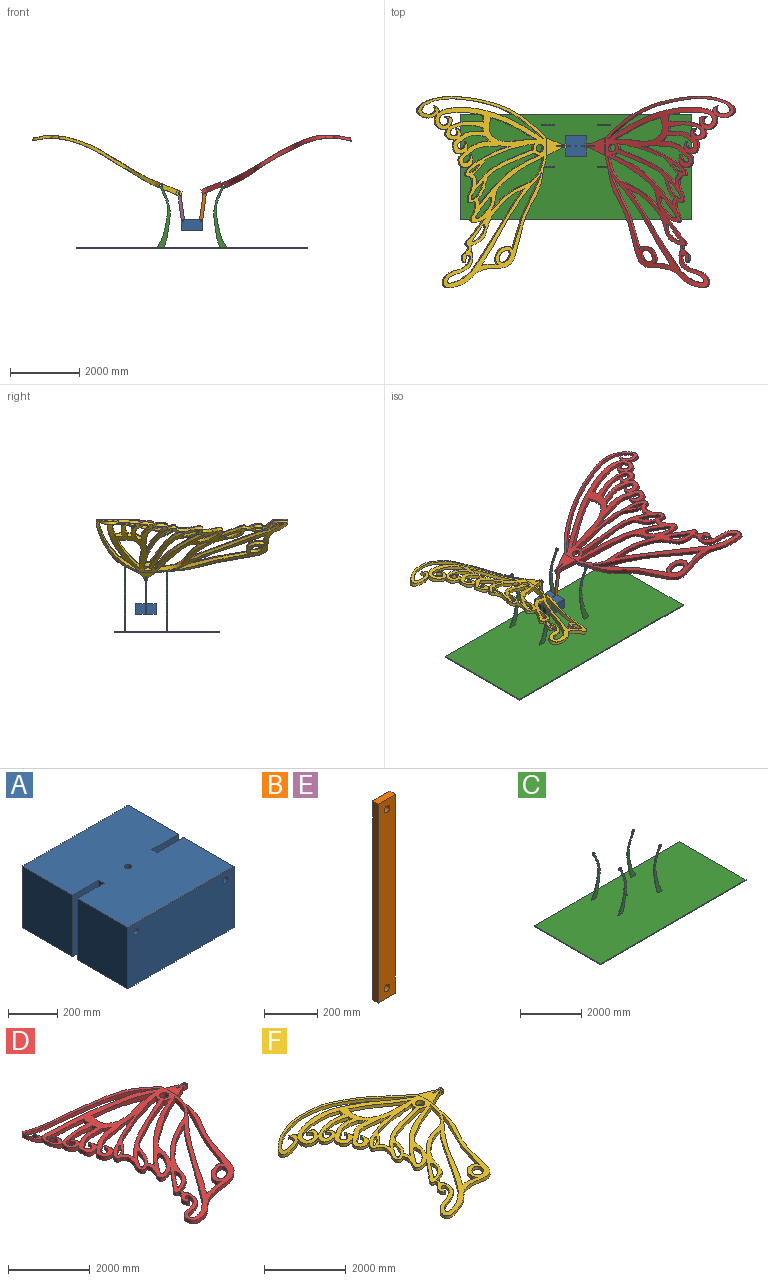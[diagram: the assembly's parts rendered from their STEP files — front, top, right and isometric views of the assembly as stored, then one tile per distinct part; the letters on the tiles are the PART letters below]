
ASSEMBLY  parts=6 mates=12
PART A: 19 faces, bbox 609.6x609.6x304.8 mm
  f0: plane 304.8x289.56mm, normal (1,0,0), area 88257.9mm2, adj f4,f6,f7,f15
  f1: plane 304.8x289.56mm, normal (-1,0,0), area 88257.9mm2, adj f4,f6,f7,f11
  f2: plane 609.6x304.8mm, normal (0,1,0), area 184346.8mm2, adj f3,f5,f6,f7,f13,f17
  f3: plane 304.8x289.56mm, normal (-1,0,0), area 88257.9mm2, adj f2,f6,f7,f10
  f4: plane 609.6x304.8mm, normal (0,-1,0), area 184346.8mm2, adj f0,f1,f6,f7,f12,f18
  f5: plane 304.8x289.56mm, normal (1,0,0), area 88257.9mm2, adj f2,f6,f7,f16
  f6: plane 609.6x609.6mm, normal (0,0,1), area 361592.2mm2, adj f0,f1,f2,f3,f4,f5,f8,f9
  f7: plane 609.6x609.6mm, normal (0,0,-1), area 361592.2mm2, adj f0,f1,f2,f3,f4,f5,f8,f9
  f8: cylinder r=15.24mm len=304.8mm, axis (0,0,1), area 29186.4mm2, adj f6,f7
  f9: plane 304.8x30.48mm, normal (-1,0,0), area 9290.3mm2, adj f6,f7,f10,f11
  f10: plane 304.8x152.4mm, normal (0,-1,0), area 45721.9mm2, adj f3,f6,f7,f9,f13
  f11: plane 304.8x152.4mm, normal (0,1,0), area 45721.9mm2, adj f1,f6,f7,f9,f12
  f12: cylinder r=15.24mm len=289.56mm, axis (0,-1,0), area 27727mm2, adj f4,f11
  f13: cylinder r=15.24mm len=289.56mm, axis (0,-1,0), area 27727mm2, adj f2,f10
  f14: plane 304.8x30.48mm, normal (1,0,0), area 9290.3mm2, adj f6,f7,f15,f16
  f15: plane 304.8x152.4mm, normal (0,1,0), area 45721.9mm2, adj f0,f6,f7,f14,f18
  f16: plane 304.8x152.4mm, normal (0,-1,0), area 45721.9mm2, adj f5,f6,f7,f14,f17
  f17: cylinder r=15.24mm len=289.56mm, axis (0,-1,0), area 27727mm2, adj f2,f16
  f18: cylinder r=15.24mm len=289.56mm, axis (0,-1,0), area 27727mm2, adj f4,f15
PART B: 8 faces, bbox 91.4x30.5x914.4 mm
  f0: plane 914.4x30.48mm, normal (-1,0,0), area 27870.9mm2, adj f1,f3,f4,f5
  f1: plane 91.44x30.48mm, normal (0,0,-1), area 2787.1mm2, adj f0,f2,f4,f5
  f2: plane 914.4x30.48mm, normal (1,0,0), area 27870.9mm2, adj f1,f3,f4,f5
  f3: plane 91.44x30.48mm, normal (0,0,1), area 2787.1mm2, adj f0,f2,f4,f5
  f4: plane 914.4x91.44mm, normal (0,-1,0), area 82153.4mm2, adj f0,f1,f2,f3,f6,f7
  f5: plane 914.4x91.44mm, normal (0,1,0), area 82153.4mm2, adj f0,f1,f2,f3,f6,f7
  f6: cylinder r=15.24mm len=30.48mm, axis (0,-1,0), area 2918.6mm2, adj f4,f5
  f7: cylinder r=15.24mm len=30.48mm, axis (0,-1,0), area 2918.6mm2, adj f4,f5
PART C: 31 faces, bbox 6705.6x3048x1884.5 mm
  f0: extruded ~1753.07x293.63mm, area 56280.8mm2, adj f9,f10,f11,f16
  f1: extruded ~1753.07x293.63mm, area 56280.8mm2, adj f2,f4,f5,f16
  f2: cylinder r=51.08mm len=102.17mm, axis (0,1,0), area 8054.2mm2, adj f1,f4,f5,f6
  f3: cylinder r=25.91mm len=51.82mm, axis (0,1,0), area 4961.7mm2, adj f4,f5
  f4: plane 1863.69x392.01mm, normal (0,-1,0), area 178526.9mm2, adj f1,f2,f3,f6,f16
  f5: plane 1863.69x392.01mm, normal (0,1,0), area 178526.9mm2, adj f1,f2,f3,f6,f16
  f6: extruded ~1771.07x243.88mm, area 56045.9mm2, adj f2,f4,f5,f16
  f7: extruded ~1771.07x243.88mm, area 56045.9mm2, adj f9,f10,f11,f16
  f8: cylinder r=25.91mm len=51.82mm, axis (0,1,0), area 4961.7mm2, adj f10,f11
  f9: cylinder r=51.08mm len=102.17mm, axis (0,1,0), area 8054.2mm2, adj f0,f7,f10,f11
  f10: plane 1863.69x392.01mm, normal (0,1,0), area 178526.9mm2, adj f0,f7,f8,f9,f16
  f11: plane 1863.69x392.01mm, normal (0,-1,0), area 178526.9mm2, adj f0,f7,f8,f9,f16
  f12: plane 6705.6x30.48mm, normal (0,1,0), area 204386.7mm2, adj f13,f15,f16,f17
  f13: plane 3048x30.48mm, normal (-1,0,0), area 92903mm2, adj f12,f14,f16,f17
  f14: plane 6705.6x30.48mm, normal (0,-1,0), area 204386.7mm2, adj f13,f15,f16,f17
  f15: plane 3048x30.48mm, normal (1,0,0), area 92903mm2, adj f12,f14,f16,f17
  f16: plane 6705.6x3048mm, normal (0,0,1), area 20414616.9mm2, adj f0,f1,f4,f5,f6,f7,f10,f11
  f17: plane 6705.6x3048mm, normal (0,0,-1), area 20437939.1mm2, adj f12,f13,f14,f15,f30
  f18: cylinder r=25.91mm len=51.82mm, axis (0,1,0), area 4961.7mm2, adj f20,f21
  f19: cylinder r=51.08mm len=102.17mm, axis (0,1,0), area 8054.2mm2, adj f20,f21,f22,f23
  f20: plane 1863.69x392.01mm, normal (0,-1,0), area 178526.9mm2, adj f16,f18,f19,f22,f23
  f21: plane 1863.69x392.01mm, normal (0,1,0), area 178526.9mm2, adj f16,f18,f19,f22,f23
  f22: extruded ~1753.07x293.63mm, area 56280.8mm2, adj f16,f19,f20,f21
  f23: extruded ~1771.07x243.88mm, area 56045.9mm2, adj f16,f19,f20,f21
  f24: cylinder r=25.91mm len=51.82mm, axis (0,1,0), area 4961.7mm2, adj f26,f27
  f25: cylinder r=51.08mm len=102.17mm, axis (0,1,0), area 8054.2mm2, adj f26,f27,f28,f29
  f26: plane 1863.69x392.01mm, normal (0,-1,0), area 178526.9mm2, adj f16,f24,f25,f28,f29
  f27: plane 1863.69x392.01mm, normal (0,1,0), area 178526.9mm2, adj f16,f24,f25,f28,f29
  f28: extruded ~1753.07x293.63mm, area 56280.8mm2, adj f16,f25,f26,f27
  f29: extruded ~1771.07x243.88mm, area 56045.9mm2, adj f16,f25,f26,f27
  f30: cylinder r=15.24mm len=30.48mm, axis (0,0,1), area 2918.6mm2, adj f16,f17
PART D: 77 faces, bbox 4569.8x5546.8x559 mm
  f0: plane 139.67x42.26mm, normal (1,0,0), area 5902.2mm2, adj f1,f2,f70,f76
  f1: plane 43.55x42.26mm, normal (0,0,1), area 1840.2mm2, adj f0,f3,f70,f76
  f2: plane 609.6x515.81mm, normal (0,0,-1), area 149908.3mm2, adj f0,f7,f68,f69,f70,f71,f72,f74
  f3: cylinder r=22.11mm len=44.21mm, axis (0,-1,0), area 3151mm2, adj f1,f4,f70,f76
  f4: plane 522.13x515.81mm, normal (0,0,1), area 143171.3mm2, adj f3,f8,f69,f70,f71,f72,f73,f74
  f5: plane 168.1x3.34mm, normal (0,-1,0), area 560.2mm2, adj f8,f23,f24,f25,f71
  f6: plane 43.55x34.77mm, normal (0,0,1), area 1514mm2, adj f7,f72,f73,f74
  f7: plane 139.67x34.77mm, normal (1,0,0), area 4855.7mm2, adj f2,f6,f72,f74
  f8: plane 515.81x80.92mm, normal (1,0,0), area 41737.8mm2, adj f4,f5,f9,f24
  f9: extruded ~3956.8x1202.56mm, area 587895.1mm2, adj f8,f10,f24,f25,f67,f69
  f10: extruded ~436.38x335.61mm, area 66062.4mm2, adj f9,f11,f24,f25
  f11: extruded ~324.15x297.79mm, area 60402.2mm2, adj f10,f13,f24,f25
  f12: extruded ~1341.39x636.81mm, area 328183.2mm2, adj f13,f14,f24,f25
  f13: extruded ~408.33x341.3mm, area 78664.2mm2, adj f11,f12,f24,f25
  f14: extruded ~320.07x163.65mm, area 32793.2mm2, adj f12,f16,f24,f25
  f15: extruded ~417.12x114.44mm, area 49528.4mm2, adj f16,f18,f24,f25
  f16: extruded ~1456.29x862.43mm, area 201626.3mm2, adj f14,f15,f24,f25
  f17: extruded ~338.56x112.28mm, area 38376.2mm2, adj f18,f19,f24,f25
  f18: extruded ~360.96x210.21mm, area 60721.4mm2, adj f15,f17,f24,f25
  f19: extruded ~451.34x277.08mm, area 82405.2mm2, adj f17,f21,f24,f25
  f20: extruded ~203.85x113.79mm, area 25603.5mm2, adj f21,f22,f24,f25
  f21: extruded ~810.37x610.36mm, area 119713.7mm2, adj f19,f20,f24,f25
  f22: extruded ~3492.14x3205.76mm, area 891755.8mm2, adj f20,f23,f24,f25
  f23: extruded ~334.69x167.83mm, area 49828.8mm2, adj f5,f22,f24,f25,f67
  f24: extruded ~5546.84x3960.16mm, area 5019713.7mm2, adj f5,f8,f9,f10,f11,f12,f13,f14
  f25: extruded ~5546.85x3960.15mm, area 5068319.2mm2, adj f5,f9,f10,f11,f12,f13,f14,f15
  f26: extruded ~371.73x350.29mm, area 115711.3mm2, adj f24,f25
  f27: extruded ~2698.77x1981.3mm, area 417691.2mm2, adj f24,f25,f29,f30
  f28: extruded ~564.75x514.56mm, area 103093.6mm2, adj f24,f25,f29,f30
  f29: extruded ~2226.78x939.05mm, area 348502.3mm2, adj f24,f25,f27,f28
  f30: extruded ~568.22x174.76mm, area 64613.8mm2, adj f24,f25,f27,f28
  f31: extruded ~175.85x107.14mm, area 19002.5mm2, adj f24,f25,f33,f34
  f32: extruded ~2372.54x1724.5mm, area 334983.2mm2, adj f24,f25,f33,f34
  f33: extruded ~1759.33x1643.13mm, area 287026.4mm2, adj f24,f25,f31,f32
  f34: extruded ~918.64x761.89mm, area 237950.4mm2, adj f24,f25,f31,f32
  f35: extruded ~486.75x409.01mm, area 149049.4mm2, adj f24,f25
  f36: extruded ~1341.6x837.92mm, area 193559.6mm2, adj f24,f25,f37,f38
  f37: extruded ~725.86x386.03mm, area 131874.2mm2, adj f24,f25,f36,f38
  f38: extruded ~1727.64x1563.78mm, area 306702.1mm2, adj f24,f25,f36,f37
  f39: extruded ~112.15x30.15mm, area 4263.4mm2, adj f24,f25,f40
  f40: extruded ~507.41x388.55mm, area 143500.5mm2, adj f24,f25,f39
  f41: cylinder r=204.59mm len=159.75mm, axis (0,0,-1), area 26058.5mm2, adj f24,f25,f43,f44
  f42: extruded ~190.19x115.16mm, area 21877.8mm2, adj f24,f25,f43,f44
  f43: extruded ~1985.13x1436.63mm, area 305854mm2, adj f24,f25,f41,f42
  f44: extruded ~1874.18x1314.28mm, area 293259.9mm2, adj f24,f25,f41,f42
  f45: extruded ~606.27x529.22mm, area 191510.7mm2, adj f24,f25
  f46: extruded ~290.04x177.88mm, area 45404.1mm2, adj f24,f25,f47,f50
  f47: cylinder r=204.59mm len=167.51mm, axis (0,0,-1), area 27142.2mm2, adj f24,f25,f46,f49
  f48: extruded ~295.93x114.32mm, area 36439.4mm2, adj f24,f25,f49,f50
  f49: extruded ~1894.48x1013.51mm, area 262807.4mm2, adj f24,f25,f47,f48
  f50: extruded ~1745.39x844.81mm, area 230263.9mm2, adj f24,f25,f46,f48
  f51: extruded ~312.12x250.36mm, area 91397mm2, adj f24,f25
  f52: extruded ~745.31x256.52mm, area 89734.6mm2, adj f24,f25,f53,f54
  f53: extruded ~874.58x425.82mm, area 183377mm2, adj f24,f25,f52,f54
  f54: extruded ~160.33x146.95mm, area 25272.4mm2, adj f24,f25,f52,f53
  f55: extruded ~727.11x153.38mm, area 82853.4mm2, adj f24,f25,f56,f57
  f56: extruded ~1000.21x334.31mm, area 207702.3mm2, adj f24,f25,f55,f57
  f57: extruded ~128.26x117.18mm, area 15039.6mm2, adj f24,f25,f55,f56
  f58: extruded ~1027.59x151.94mm, area 115311.2mm2, adj f24,f25,f59,f60
  f59: extruded ~1342.84x408.07mm, area 267599.7mm2, adj f24,f25,f58,f60
  f60: extruded ~193.21x117.8mm, area 22533.7mm2, adj f24,f25,f58,f59
  f61: cylinder r=111mm len=222.01mm, axis (0,0,-1), area 108573.6mm2, adj f24,f25
  f62: extruded ~1571.66x697.24mm, area 254753.4mm2, adj f24,f25,f63
  f63: extruded ~1515.88x632.2mm, area 207996mm2, adj f24,f25,f62
  f64: extruded ~3775.49x1155.09mm, area 548964.1mm2, adj f24,f25,f65,f66
  f65: extruded ~206.26x146.99mm, area 24674.3mm2, adj f24,f25,f64,f66
  f66: extruded ~3350.46x907.58mm, area 430785.2mm2, adj f24,f25,f64,f65
  f67: cylinder r=24.38mm len=859.93mm, axis (0,-1,0), area 114966.2mm2, adj f9,f23
  f68: plane 515.81x52.49mm, normal (-1,0,0), area 27075mm2, adj f2,f25,f69,f71
  f69: plane 456.44x178.06mm, normal (0.36,0.93,0), area 68430.7mm2, adj f2,f4,f9,f68,f70
  f70: plane 153.16x139.67mm, normal (0,1,0), area 20511.9mm2, adj f0,f1,f2,f3,f4,f69
  f71: plane 460.62x230.25mm, normal (0.45,-0.89,0), area 71925.1mm2, adj f2,f4,f5,f68,f72
  f72: plane 148.98x139.67mm, normal (0,-1,0), area 19928.3mm2, adj f2,f4,f6,f7,f71,f73
  f73: cylinder r=22.11mm len=44.21mm, axis (0,-1,0), area 2592.3mm2, adj f4,f6,f72,f74
  f74: plane 304.8x139.67mm, normal (0,1,0), area 41691.6mm2, adj f2,f4,f6,f7,f73,f75
  f75: plane 139.67x30.48mm, normal (1,0,0), area 4257.2mm2, adj f2,f4,f74,f76
  f76: plane 304.8x139.67mm, normal (0,-1,0), area 41691.6mm2, adj f0,f1,f2,f3,f4,f75
PART E: same geometry as B
PART F: 73 faces, bbox 4569.8x5546.8x534.1 mm
  f0: plane 139.67x43.35mm, normal (1,0,0), area 6054.7mm2, adj f3,f4,f68,f71
  f1: cylinder r=22.11mm len=44.21mm, axis (0,-1,0), area 6021.4mm2, adj f68,f71
  f2: plane 139.67x3.34mm, normal (0,-1,0), area 465.5mm2, adj f20,f21,f22,f67
  f3: plane 609.6x515.81mm, normal (0,0,1), area 149908.3mm2, adj f0,f5,f21,f65,f66,f67,f68,f70
  f4: plane 609.6x515.81mm, normal (0,0,-1), area 149908.3mm2, adj f0,f5,f22,f65,f66,f67,f68,f70
  f5: plane 139.67x33.67mm, normal (1,0,0), area 4703.2mm2, adj f3,f4,f66,f70
  f6: extruded ~3956.8x1202.56mm, area 479492.5mm2, adj f7,f21,f22,f64,f65
  f7: extruded ~436.38x335.61mm, area 59997.6mm2, adj f6,f8,f21,f22
  f8: extruded ~324.15x297.79mm, area 45490mm2, adj f7,f10,f21,f22
  f9: extruded ~1341.39x636.81mm, area 262319.7mm2, adj f10,f11,f21,f22
  f10: extruded ~408.33x341.3mm, area 55795.2mm2, adj f8,f9,f21,f22
  f11: extruded ~320.07x139.67mm, area 30654.5mm2, adj f9,f13,f21,f22
  f12: extruded ~417.12x114.44mm, area 41974.9mm2, adj f13,f15,f21,f22
  f13: extruded ~1456.29x862.43mm, area 170075.6mm2, adj f11,f12,f21,f22
  f14: extruded ~338.56x95.61mm, area 33270.6mm2, adj f15,f16,f21,f22
  f15: extruded ~360.96x210.21mm, area 50245.5mm2, adj f12,f14,f21,f22
  f16: extruded ~451.34x277.08mm, area 69924.5mm2, adj f14,f18,f21,f22
  f17: extruded ~203.85x113.79mm, area 20376.9mm2, adj f18,f19,f21,f22
  f18: extruded ~810.37x610.36mm, area 99648.6mm2, adj f16,f17,f21,f22
  f19: extruded ~3492.14x3205.76mm, area 673396.6mm2, adj f17,f20,f21,f22
  f20: extruded ~334.69x139.47mm, area 40369.6mm2, adj f2,f19,f21,f22,f64
  f21: extruded ~5546.84x3960.15mm, area 4961774.6mm2, adj f2,f3,f6,f7,f8,f9,f10,f11
  f22: extruded ~5546.84x3960.13mm, area 5066569.9mm2, adj f2,f4,f6,f7,f8,f9,f10,f11
  f23: extruded ~371.73x350.29mm, area 107130.3mm2, adj f21,f22
  f24: extruded ~2698.77x1981.3mm, area 327186.9mm2, adj f21,f22,f26,f27
  f25: extruded ~564.75x514.56mm, area 91953.3mm2, adj f21,f22,f26,f27
  f26: extruded ~2226.78x939.05mm, area 247754.4mm2, adj f21,f22,f24,f25
  f27: extruded ~568.22x180.29mm, area 52584.8mm2, adj f21,f22,f24,f25
  f28: extruded ~175.85x89.85mm, area 16005.1mm2, adj f21,f22,f30,f31
  f29: extruded ~2372.54x1724.5mm, area 273784.5mm2, adj f21,f22,f30,f31
  f30: extruded ~1759.33x1643.13mm, area 233997.2mm2, adj f21,f22,f28,f29
  f31: extruded ~918.64x761.89mm, area 181893.8mm2, adj f21,f22,f28,f29
  f32: extruded ~486.75x409.01mm, area 125793mm2, adj f21,f22
  f33: extruded ~1341.6x837.92mm, area 150356.5mm2, adj f21,f22,f34,f35
  f34: extruded ~725.86x386.03mm, area 106314.3mm2, adj f21,f22,f33,f35
  f35: extruded ~1727.64x1563.78mm, area 241201.2mm2, adj f21,f22,f33,f34
  f36: extruded ~96.94x30.15mm, area 3705.4mm2, adj f21,f22,f37
  f37: extruded ~507.41x388.55mm, area 122345.4mm2, adj f21,f22,f36
  f38: cylinder r=204.59mm len=150.41mm, axis (0,0,-1), area 20703.4mm2, adj f21,f22,f40,f41
  f39: extruded ~190.19x99.54mm, area 18856mm2, adj f21,f22,f40,f41
  f40: extruded ~1985.13x1436.63mm, area 239417.2mm2, adj f21,f22,f38,f39
  f41: extruded ~1874.18x1314.28mm, area 229002mm2, adj f21,f22,f38,f39
  f42: extruded ~606.27x529.22mm, area 156728mm2, adj f21,f22
  f43: extruded ~290.04x131.49mm, area 30372mm2, adj f21,f22,f44,f47
  f44: cylinder r=204.59mm len=167.51mm, axis (0,0,-1), area 20268mm2, adj f21,f22,f43,f46
  f45: extruded ~295.93x100.85mm, area 31601.3mm2, adj f21,f22,f46,f47
  f46: extruded ~1894.48x1013.51mm, area 205802.1mm2, adj f21,f22,f44,f45
  f47: extruded ~1745.39x844.81mm, area 186541.1mm2, adj f21,f22,f43,f45
  f48: extruded ~312.12x250.36mm, area 78192.5mm2, adj f21,f22
  f49: extruded ~745.31x256.52mm, area 74485.5mm2, adj f21,f22,f50,f51
  f50: extruded ~874.58x425.82mm, area 142766.4mm2, adj f21,f22,f49,f51
  f51: extruded ~160.33x146.95mm, area 19914.5mm2, adj f21,f22,f49,f50
  f52: extruded ~727.11x153.38mm, area 67474mm2, adj f21,f22,f53,f54
  f53: extruded ~1000.21x334.31mm, area 155554.5mm2, adj f21,f22,f52,f54
  f54: extruded ~128.26x97.61mm, area 12386.4mm2, adj f21,f22,f52,f53
  f55: extruded ~1027.59x145.28mm, area 90164.4mm2, adj f21,f22,f56,f57
  f56: extruded ~1342.84x408.07mm, area 208962.4mm2, adj f21,f22,f55,f57
  f57: extruded ~193.21x98.15mm, area 18512mm2, adj f21,f22,f55,f56
  f58: cylinder r=111mm len=222.01mm, axis (0,0,-1), area 88758.8mm2, adj f21,f22
  f59: extruded ~1571.66x697.24mm, area 196238.7mm2, adj f21,f22,f60
  f60: extruded ~1515.88x632.2mm, area 158574.1mm2, adj f21,f22,f59
  f61: extruded ~3775.49x1155.09mm, area 455207.2mm2, adj f21,f22,f62,f63
  f62: extruded ~206.26x134.16mm, area 22998.4mm2, adj f21,f22,f61,f63
  f63: extruded ~3350.46x907.58mm, area 336360.7mm2, adj f21,f22,f61,f62
  f64: cylinder r=24.38mm len=863.62mm, axis (0,-1,0), area 115665.8mm2, adj f6,f20
  f65: plane 456.44x178.06mm, normal (0.36,0.93,0), area 68430.7mm2, adj f3,f4,f6,f66
  f66: plane 153.16x139.67mm, normal (0,1,0), area 19856.8mm2, adj f3,f4,f5,f65,f69
  f67: plane 460.62x230.25mm, normal (0.45,-0.89,0), area 71925.1mm2, adj f2,f3,f4,f68
  f68: plane 148.98x139.67mm, normal (0,-1,0), area 19273.2mm2, adj f0,f1,f3,f4,f67
  f69: cylinder r=22.11mm len=44.21mm, axis (0,-1,0), area 4677.4mm2, adj f66,f70
  f70: plane 304.8x139.67mm, normal (0,-1,0), area 41036.5mm2, adj f3,f4,f5,f69,f72
  f71: plane 304.8x139.67mm, normal (0,1,0), area 41036.5mm2, adj f0,f1,f3,f4,f72
  f72: plane 139.67x30.48mm, normal (1,0,0), area 4257.2mm2, adj f3,f4,f70,f71
PLACE A t=(887.34,2000.77,971.84)mm
PLACE B rot(axis=(0,1,0),8.2deg) t=(1092.31,2016.01,1194.62)mm
PLACE C t=(887.34,1391.17,437.88)mm fixed
PLACE D rot(axis=(0,1,0),157.6deg) t=(1630.28,2236.32,2581.25)mm
PLACE E rot(axis=(0,-1,0),7.9deg) t=(591.58,2016.01,1181.74)mm
PLACE F rot(axis=(0,1,0),22.6deg) t=(-98.75,2227.74,1991.65)mm
MATE cylindrical C.f30 <-> A.f8  axis (0,0,1) through (887.34,2000.77,453.12)mm
MATE planar B.f6 <-> D.f74  axis (0,-1,0) through (1261.98,1985.53,2047.79)mm
MATE parallel A.f6 <-> C.f16  axis (0,0,1) through (1039.74,1985.53,1276.64)mm
MATE planar F.f70 <-> A.f10  axis (0,-1,0) through (429.68,2016.01,2080.73)mm
MATE cylindrical E.f6 <-> F.f1  axis (0,-1,0) through (517.25,2000.77,2048.44)mm
MATE planar D.f3 <-> A.f16  axis (0,-1,0) through (1261.98,2016.01,2047.79)mm
MATE cylindrical C.f2 <-> D.f67  axis (0,1,0) through (1802.83,2625.61,2271.34)mm
MATE cylindrical E.f7 <-> A.f12  axis (0,-1,0) through (630.57,1985.53,1233.32)mm
MATE cylindrical B.f6 <-> D.f3  axis (0,-1,0) through (1261.98,1985.53,2047.79)mm
MATE cylindrical F.f64 <-> C.f8  axis (0,-1,0) through (-28.14,1421.21,2271.34)mm
MATE cylindrical A.f17 <-> B.f7  axis (0,-1,0) through (1144.11,2160.79,1233.32)mm
MATE planar E.f4 <-> A.f11  axis (0,-1,0) through (573.91,1985.53,1640.88)mm
